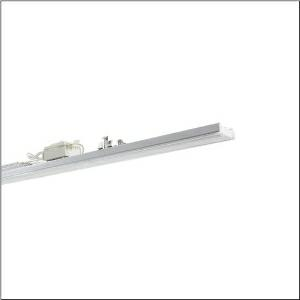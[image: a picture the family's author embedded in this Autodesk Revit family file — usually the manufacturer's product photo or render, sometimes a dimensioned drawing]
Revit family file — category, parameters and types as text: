
# Revit family: licross_r__21_recessed_ho_52tl1ecn4cxs_20c2
name_source: partatom
category: Lighting Fixtures
units: mm (PartAtom-declared; Revit-internal decimal feet)

## family parameters
Cut with Voids When Loaded = No
Host = Face
Light Source = No
Part Type = Normal
Room Calculation Point = No
Round Connector Dimension = Use Diameter
Shared = No

## types (1)
- --- (1 x LED, 12350 lm, 68.4 W, 4000K)
    Apparent Load = 68 VA
    CIE Flux Codes = 85 95 99 100 100
    Color Rendering = 80
    Color Temperature = 4000K
    Default Elevation = 1800 mm
    Description = Licross® 21 Recessed HO, luminaire insert, of sheet steel, galvanised, coil coated, white, length: 1.500mm, width: 66mm, height: 67mm, LED rated luminous flux: 12.350lm, light colour: 840, control gear: ON/OFF Multilumen, CLOi, control gear: ECG Multilumen, with plug, 3-pole, with phase selection, mains connection: 220..240V, AC, 50/60Hz, start of lifetime: 69W, end of service life: 83W, halogen-free wiring, primary light control with lens, of plastic, primary optical cover: cover, of PMMA, light emission: direct distribution, primary light characteristic: symmetric, protection rating (complete): IP40, insulation class (complete): insulation class I (protective earthing), certification: CE, ENEC, VDE, UKCA, protection symbol: D if used in an environment without relevant dust loads with corresponding accessories, impact resistance: IK06, permissible ambient temperature for indoor applications: -35..+30°C, corresponds to IFS (International Featured Standards) requirements for safety and quality in the food industry, reducing of maximum allowable ambient temperature of 5°C with ceiling mounting, LABS conformity tested according to VDMA 24364:2018-05, packaging unit: 1 piece
    Height = 58 mm
    Lamp = 1 x LED
    Lamp Light Flux = 12350 lm
    Lamp Power = 68.4 W
    Lamp count = 1
    Length = 1500 mm
    Luminous efficacy = 181 lm/W
    Manufacturer = Siteco
    ModVariant = No
    Model = 52TL1ECN4CXS
    Mounting Place = Ceiling
    Mounting Type = Pendant
    Number of Poles = 1
    OnlyDefault = Yes
    Power Factor = 1
    Product Name = Licross® 21 Recessed HO
    Product group = luminaire insert
    ProductGroupID = 902
    Protection Class = Protection class I
    Protection Degree = IP 40
    RLX_Detail_Level = 1
    RLX_Emergency_Light_Flux = 0 lm
    RLX_Emergency_Type = 0
    RLX_Emergency_Type_DB = No
    RlxData = <blob elided: 22461 chars, md5=39fb768d>
    Socket = socket
    Standby Power = 0 W
    System Light Flux = 12350 lm
    System Power = 68 W
    Type Comments = factory setting: luminous flux: 100 % | (A | C | E) | 161 mA
    Type Image = l_1296930.jpg
    URL = http://relux.com
    VarID = @adj_109938
    Voltage = 0 V
    Weight = 0.00 kg
    Width = 66 mm

## geometry (parser evidence)
native form markers: Blend x4, Sweep x9
no freeform markers — native parametric forms only
